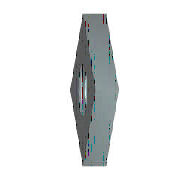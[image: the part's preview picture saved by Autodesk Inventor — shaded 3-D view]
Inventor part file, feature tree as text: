
AUTODESK INVENTOR PART (.ipt)
format: ipt  version: 2018 (Build 220112000, 112)  size: 124,416 bytes
history: native  units: mm (DEFAULTED — no unit token found)
features: sketch x2, hole x1, other x1, plane x1
ambient origin geometry x8: Origin, YZ Plane, XZ Plane, XY Plane, X Axis, Y Axis, Z Axis, Center Point
bodies: Solid1 (feature_tree), Body (feature_tree)
feature tree (5):
  hole  "Thread"  [1 undecoded]
  other  "Work Axis1"
  plane  "Work Plane1"
  sketch  "Sketch1"  dims[d0=7.778175mm d1=1.78mm d2=0.0mm]
  sketch  "Sketch2"  dims[d20=2.459mm d21=6.0mm d22=4.0mm d23=2.0mm d24=14.3117mm d25=8.0mm d26=20.594885mm d3=0.270633mm d4=30.0deg d5=0.270633mm d6=30.0deg d8=0.0mm d9=0.0mm d34=0.0mm d35=0.270633mm d36=0.270633mm d37=90.0deg d38=0.0mm]
note: 1 required parameter value undecoded (feature->parameter linkage not recoverable at this tier; creation-order binding heuristic only, values carry confidence <= 0.55)
